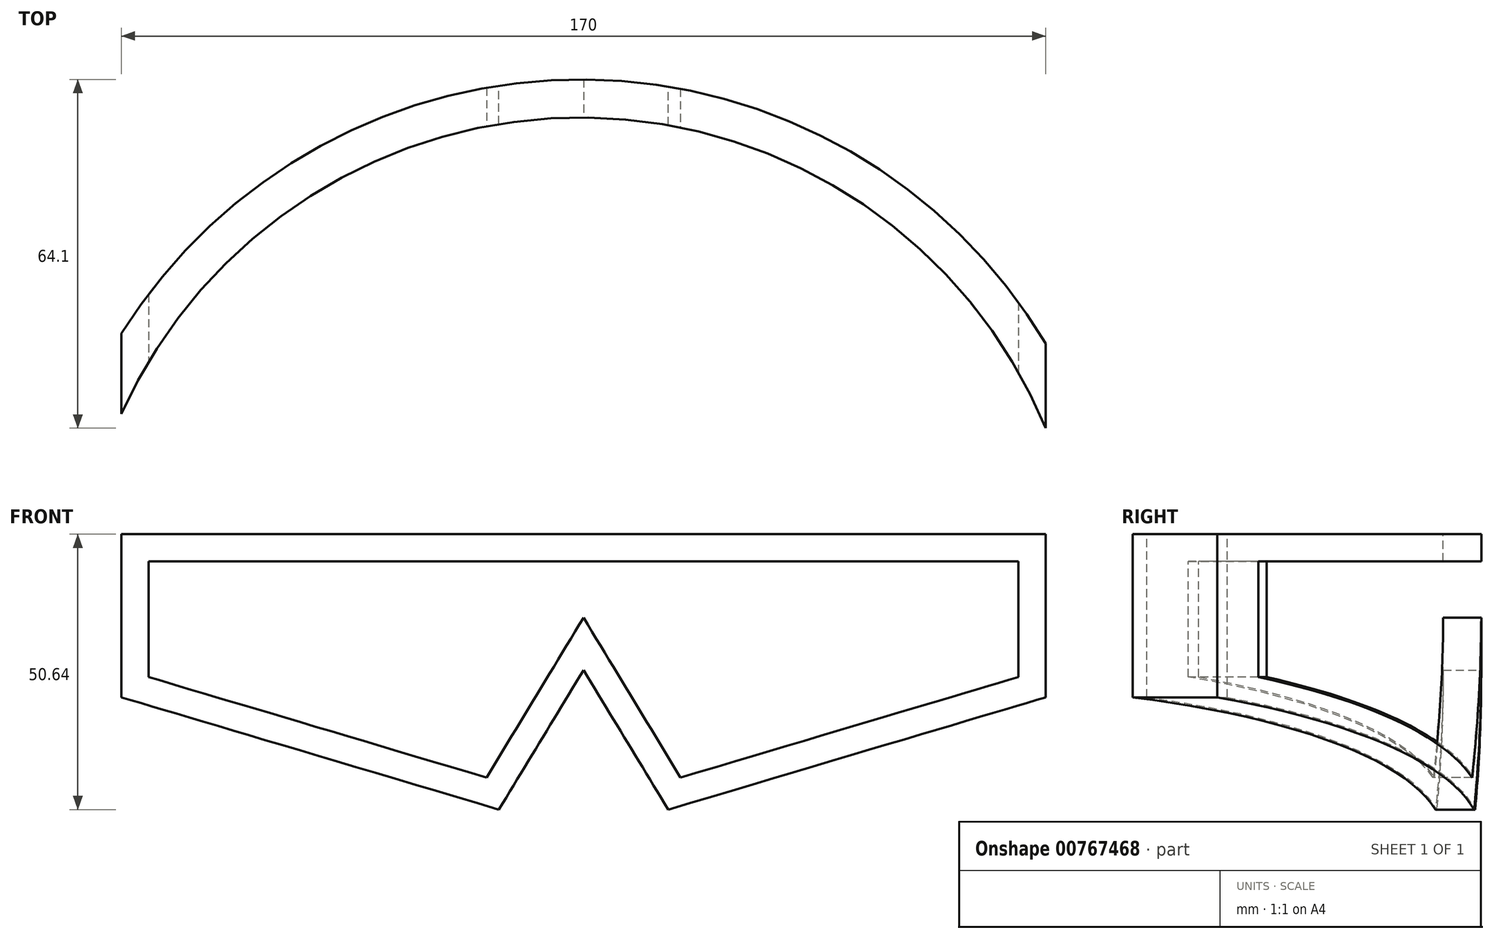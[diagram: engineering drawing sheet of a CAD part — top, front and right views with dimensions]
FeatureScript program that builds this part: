
annotation { "Feature Type Name" : "Feature", "Feature Type Description" : "" }
export const myFeature = defineFeature(function(context is Context, id is Id, definition is map)
    precondition{}
    {
        {
            var Q0;
            Q0=qCreatedBy(makeId("Front.planeOp"),FACE);
            var sketch = newSketch(context, id + "F0", { "sketchPlane" : qUnion([Q0])});
            skLineSegment(sketch, "E0.top", {"start": v(0.3, 25.88) * mm, "end": v(-84.7, 25.88) * mm});
            skLineSegment(sketch, "E0.right", {"start": v(-84.7, -4.12) * mm, "end": v(-84.7, 25.88) * mm});
            skPoint(sketch, "E0.middle", {"position": v(-42.2, -4.6) * mm});
            skLineSegment(sketch, "E1", {"start": v(-15.27, -24.76) * mm, "end": v(0.3, 0.88) * mm});
            skLineSegment(sketch, "E2", {"start": v(-15.27, -24.76) * mm, "end": v(-84.7, -4.12) * mm});
            skPoint(sketch, "E3.orphan", {"position": v(-84.7, -35.08) * mm});
            skPoint(sketch, "E4.orphan", {"position": v(0.3, -35.08) * mm});
            skPoint(sketch, "E5.middle", {"position": v(0.94, 33.45) * mm});
            skPoint(sketch, "E6.orphan", {"position": v(-41.56, 5.6) * mm});
            skPoint(sketch, "E7.orphan", {"position": v(43.44, 5.6) * mm});
            skLineSegment(sketch, "E8.MirrorCS", {"start": v(15.87, -24.76) * mm, "end": v(0.3, 0.88) * mm});
            skLineSegment(sketch, "E9.MirrorCS", {"start": v(15.87, -24.76) * mm, "end": v(85.3, -4.12) * mm});
            skLineSegment(sketch, "E10.MirrorCS", {"start": v(85.3, -4.12) * mm, "end": v(85.3, 25.88) * mm});
            skLineSegment(sketch, "E11.MirrorCS", {"start": v(0.3, 25.88) * mm, "end": v(85.3, 25.88) * mm});
            skPoint(sketch, "E12.orphan", {"position": v(-87.16, -3.39) * mm});
            skPoint(sketch, "E13.orphan", {"position": v(87.76, -3.39) * mm});
            skSolve(sketch);
        }
        {
            var Q0;
            Q0=qSketchRegion(id+"F0",true);
            extrude(context, id + "F1", {"entities" : qUnion([Q0]), "endBound" : BoundingType.SYMMETRIC, "depth" : 150 * mm, "offsetDistance" : 25 * mm});
        }
        {
            var Q0;
            Q0=makeQuery(id+"F1.opExtrude","CAP_FACE",FACE,{"disambiguationData":[OSD([sQuery(id+"F0.wireOp",EDGE,"E0.top"),sQuery(id+"F0.wireOp",EDGE,"E0.right"),sQuery(id+"F0.wireOp",EDGE,"E1"),sQuery(id+"F0.wireOp",EDGE,"E2"),sQuery(id+"F0.wireOp",EDGE,"E8.MirrorCS"),sQuery(id+"F0.wireOp",EDGE,"E9.MirrorCS"),sQuery(id+"F0.wireOp",EDGE,"E10.MirrorCS"),sQuery(id+"F0.wireOp",EDGE,"E11.MirrorCS")])],"isStart":false});
            var sketch = newSketch(context, id + "F2", { "sketchPlane" : qUnion([Q0])});
            skLineSegment(sketch, "E14.0", {"start": v(0.3, 10.52) * mm, "end": v(18.14, -18.87) * mm});
            skLineSegment(sketch, "E14.1", {"start": v(-17.54, -18.87) * mm, "end": v(0.3, 10.52) * mm});
            skLineSegment(sketch, "E14.2", {"start": v(80.3, -0.39) * mm, "end": v(80.3, 20.88) * mm});
            skLineSegment(sketch, "E14.3", {"start": v(80.3, 20.88) * mm, "end": v(-79.7, 20.88) * mm});
            skLineSegment(sketch, "E14.4", {"start": v(-79.7, 20.88) * mm, "end": v(-79.7, -0.39) * mm});
            skLineSegment(sketch, "E14.5", {"start": v(18.14, -18.87) * mm, "end": v(80.3, -0.39) * mm});
            skLineSegment(sketch, "E14.6", {"start": v(-79.7, -0.39) * mm, "end": v(-17.54, -18.87) * mm});
            skSolve(sketch);
        }
        {
            var Q0;
            Q0=qSketchRegion(id+"F2",true);
            extrude(context, id + "F3", {"entities" : qUnion([Q0]), "operationType" : NewBodyOperationType.REMOVE, "oppositeDirection" : true, "depth" : 200 * mm, "offsetDistance" : 25 * mm});
        }
        {
            var Q0;
            Q0=makeQuery(id+"F1.opExtrude","SWEPT_FACE",FACE,{"disambiguationData":[OSD([sQuery(id+"F0.wireOp",EDGE,"E0.top"),sQuery(id+"F0.wireOp",EDGE,"E11.MirrorCS")])]});
            var sketch = newSketch(context, id + "F4", { "sketchPlane" : qUnion([Q0])});
            skArc(sketch, "E15", {"start": v(99.3, -26.96) * mm, "mid": v(-3.95, 68.28) * mm, "end": v(-99.88, -34.33) * mm});
            skArc(sketch, "E16.0", {"start": v(92.3, -27.27) * mm, "mid": v(-3.7, 61.29) * mm, "end": v(-92.88, -34.12) * mm});
            skLineSegment(sketch, "E17", {"start": v(-99.88, -34.33) * mm, "end": v(-92.88, -34.12) * mm});
            skLineSegment(sketch, "E18", {"start": v(92.3, -27.27) * mm, "end": v(99.3, -26.96) * mm});
            skSolve(sketch);
        }
        {
            var Q0;
            Q0=qSketchRegion(id+"F4",true);
            extrude(context, id + "F5", {"entities" : qUnion([Q0]), "operationType" : NewBodyOperationType.INTERSECT, "oppositeDirection" : true, "depth" : 100 * mm, "offsetDistance" : 25 * mm});
        }
    });
